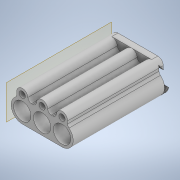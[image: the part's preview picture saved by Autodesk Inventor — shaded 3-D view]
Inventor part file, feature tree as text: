
AUTODESK INVENTOR PART (.ipt)
format: ipt  version: 2022.3 (Build 263350000, 350)  size: 201,216 bytes
history: mixed  units: in
note: dims shown in document units (in); Inventor stores cm internally (conversion verified against a paired STEP export)
features: extrude x3, sketch x2, thicken_offset x1, plane x1, projected_geometry x1, imported_body x1
ambient origin geometry x8: Origin, YZ Plane, XZ Plane, XY Plane, X Axis, Y Axis, Z Axis, Center Point
bodies: Solid1 (imported_parasolid), Body1 (imported_parasolid)
feature tree (9):
  thicken_offset  "Thicken1"
  plane  "Work Plane1"
  sketch  "Sketch1"  dims[d0=0.5906in d1=0.5906in]
  extrude  "Extrusion1"  Depth=0.5906in
  extrude  "Extrusion2"  Depth=0.9843in
  extrude  "Extrusion3"  Depth=0.1378in
  sketch  "Sketch2"  dims[d2=-0.3543in d3=0.9843in d4=0.1378in d5=0.7874in d6=0.2756in d7=0.1969in d8=0.1969in d9=0.0591in d10=0.3937in d11=0.0in d12=0.3937in d13=0.0in d14=0.0in d15=0.0in]
  projected_geometry  "Projected Loop1"
  imported_body  NMx_Import_Brep_tag  [imported B-rep: ~43 faces, bbox_mm=[49.748239, 25.0, 77.0]]
